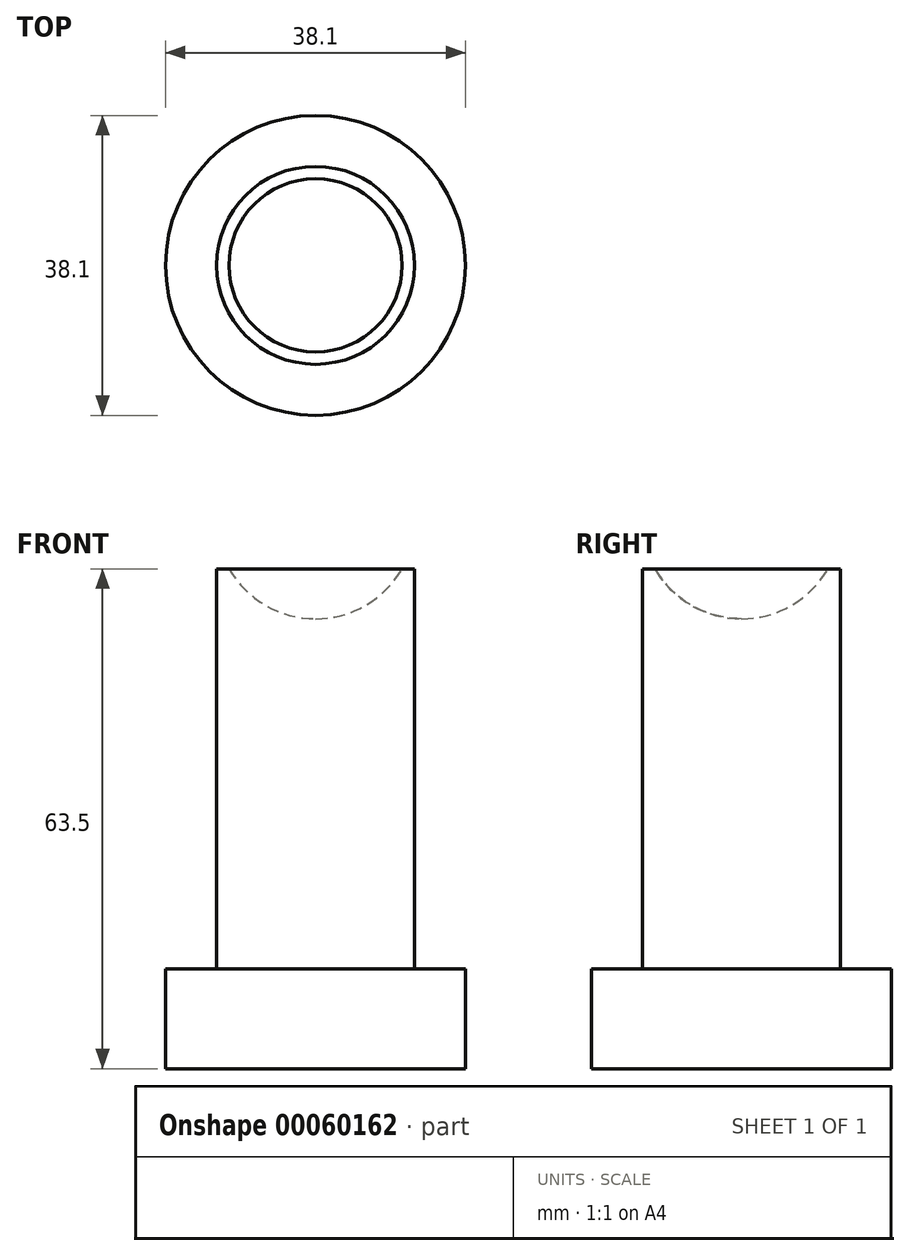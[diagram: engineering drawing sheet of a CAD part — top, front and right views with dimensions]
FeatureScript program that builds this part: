
annotation { "Feature Type Name" : "Feature", "Feature Type Description" : "" }
export const myFeature = defineFeature(function(context is Context, id is Id, definition is map)
    precondition{}
    {
        {
            var Q0;
            Q0=qCreatedBy(makeId("Top.planeOp"),FACE);
            var sketch = newSketch(context, id + "F0", { "sketchPlane" : qUnion([Q0])});
            skCircle(sketch, "E0", {"center": v(0, 0) * mm, "radius": 19.05 * mm});
            skSolve(sketch);
        }
        {
            var Q0;
            Q0=makeQuery(id+"F0.imprint","IMPRINT",FACE,{"disambiguationData":[TD([[makeQuery(id+"F0.imprint","IMPRINT",EDGE,{"derivedFrom":sQuery(id+"F0.wireOp",EDGE,"E0")}),1.0]])]});
            extrude(context, id + "F1", {"entities" : qUnion([Q0]), "oppositeDirection" : true, "depth" : 12.7 * mm});
        }
        {
            var Q0;
            Q0=makeQuery(id+"F1.opExtrude","CAP_FACE",FACE,{"disambiguationData":[OSD([sQuery(id+"F0.wireOp",EDGE,"E0")])],"isStart":true});
            var sketch = newSketch(context, id + "F2", { "sketchPlane" : qUnion([Q0])});
            skCircle(sketch, "E1", {"center": v(0, 0) * mm, "radius": 12.57 * mm});
            skSolve(sketch);
        }
        {
            var Q0;
            Q0=makeQuery(id+"F2.imprint","IMPRINT",FACE,{"disambiguationData":[TD([[makeQuery(id+"F2.imprint","IMPRINT",EDGE,{"derivedFrom":sQuery(id+"F2.wireOp",EDGE,"E1")}),1.0]])]});
            extrude(context, id + "F3", {"entities" : qUnion([Q0]), "operationType" : NewBodyOperationType.ADD, "depth" : 50.8 * mm});
        }
        {
            var Q0;
            Q0=qCreatedBy(makeId("Right.planeOp"),FACE);
            var sketch = newSketch(context, id + "F4", { "sketchPlane" : qUnion([Q0])});
            skArc(sketch, "E2", {"start": v(11, 50.8) * mm, "mid": v(6.35, 46.15) * mm, "end": v(0, 44.45) * mm});
            skLineSegment(sketch, "E3", {"start": v(0, 44.45) * mm, "end": v(0, 50.8) * mm});
            skLineSegment(sketch, "E4", {"start": v(0, 50.8) * mm, "end": v(11, 50.8) * mm});
            skSolve(sketch);
        }
        {
            var Q0;
            Q0 = qSketchRegion(id + "F4", true);
            var Q1;
            Q1=sQuery(id+"F4.wireOp",EDGE,"E3");
            revolve(context, id + "F5", {"operationType" : NewBodyOperationType.REMOVE, "entities" : qUnion([Q0]), "axis" : qUnion([Q1]), "revolveType" : RevolveType.FULL, "oppositeDirection" : true});
        }
    });
